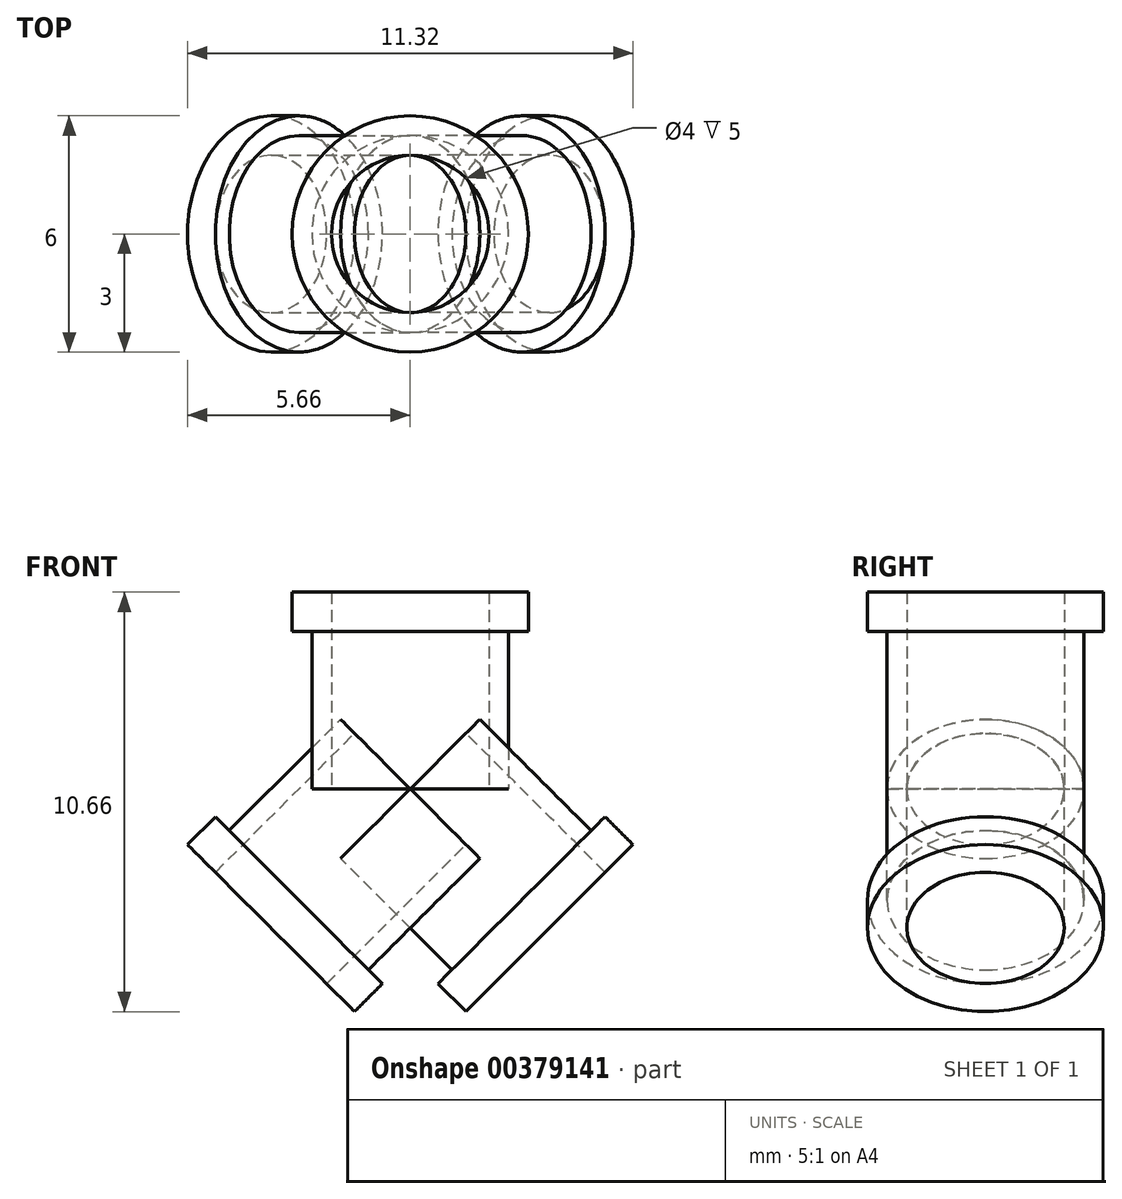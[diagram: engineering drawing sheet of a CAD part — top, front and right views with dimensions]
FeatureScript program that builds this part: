
annotation { "Feature Type Name" : "Feature", "Feature Type Description" : "" }
export const myFeature = defineFeature(function(context is Context, id is Id, definition is map)
    precondition{}
    {
        {
            var Q0;
            Q0=qCreatedBy(makeId("Front.planeOp"),FACE);
            var sketch = newSketch(context, id + "F0", { "sketchPlane" : qUnion([Q0])});
            skLineSegment(sketch, "E0", {"start": v(0, 0) * mm, "end": v(0, 24.98) * mm, "construction": true});
            skLineSegment(sketch, "E1", {"start": v(2, 5) * mm, "end": v(3, 5) * mm});
            skLineSegment(sketch, "E2", {"start": v(3, 5) * mm, "end": v(3, 4) * mm});
            skLineSegment(sketch, "E3", {"start": v(3, 4) * mm, "end": v(2.5, 4) * mm});
            skLineSegment(sketch, "E4", {"start": v(2.5, 4) * mm, "end": v(2.5, 0) * mm});
            skLineSegment(sketch, "E5", {"start": v(2.5, 0) * mm, "end": v(2, 0) * mm});
            skLineSegment(sketch, "E6", {"start": v(2, 0) * mm, "end": v(2, 5) * mm});
            skSolve(sketch);
        }
        {
            var Q0;
            Q0=makeQuery(id+"F0.imprint","IMPRINT",FACE,{"disambiguationData":[TD([[makeQuery(id+"F0.imprint","IMPRINT",EDGE,{"derivedFrom":sQuery(id+"F0.wireOp",EDGE,"E1")}),-1.0]])]});
            var Q1;
            Q1=sQuery(id+"F0.wireOp",EDGE,"E0");
            revolve(context, id + "F1", {"entities" : qUnion([Q0]), "axis" : qUnion([Q1]), "revolveType" : RevolveType.FULL});
        }
        {
            var Q0;
            Q0=qCreatedBy(makeId("Top.planeOp"),FACE);
            var sketch = newSketch(context, id + "F2", { "sketchPlane" : qUnion([Q0])});
            skLineSegment(sketch, "E7", {"start": v(0, 0) * mm, "end": v(0, -21.1) * mm, "construction": true});
            skSolve(sketch);
        }
        {
            var Q0;
            Q0=makeQuery(id+"F1.opRevolve","SWEPT_BODY",BODY,{"disambiguationData":[OSD([sQuery(id+"F0.wireOp",EDGE,"E1"),sQuery(id+"F0.wireOp",EDGE,"E2"),sQuery(id+"F0.wireOp",EDGE,"E3"),sQuery(id+"F0.wireOp",EDGE,"E4"),sQuery(id+"F0.wireOp",EDGE,"E5"),sQuery(id+"F0.wireOp",EDGE,"E6")])]});
            var Q1;
            Q1=sQuery(id+"F2.wireOp",EDGE,"E7");
            transform(context, id + "F3", {"entities" : qUnion([Q0]), "transformType" : TransformType.ROTATION, "transformAxis" : qUnion([Q1]), "angle" : 135 * degree, "makeCopy" : true});
        }
        {
            var Q0;
            Q0=makeQuery(id+"F1.opRevolve","SWEPT_BODY",BODY,{"disambiguationData":[OSD([sQuery(id+"F0.wireOp",EDGE,"E1"),sQuery(id+"F0.wireOp",EDGE,"E2"),sQuery(id+"F0.wireOp",EDGE,"E3"),sQuery(id+"F0.wireOp",EDGE,"E4"),sQuery(id+"F0.wireOp",EDGE,"E5"),sQuery(id+"F0.wireOp",EDGE,"E6")])]});
            var Q1;
            Q1=sQuery(id+"F2.wireOp",EDGE,"E7");
            transform(context, id + "F4", {"entities" : qUnion([Q0]), "transformType" : TransformType.ROTATION, "transformAxis" : qUnion([Q1]), "angle" : 225 * degree, "makeCopy" : true});
        }
    });
